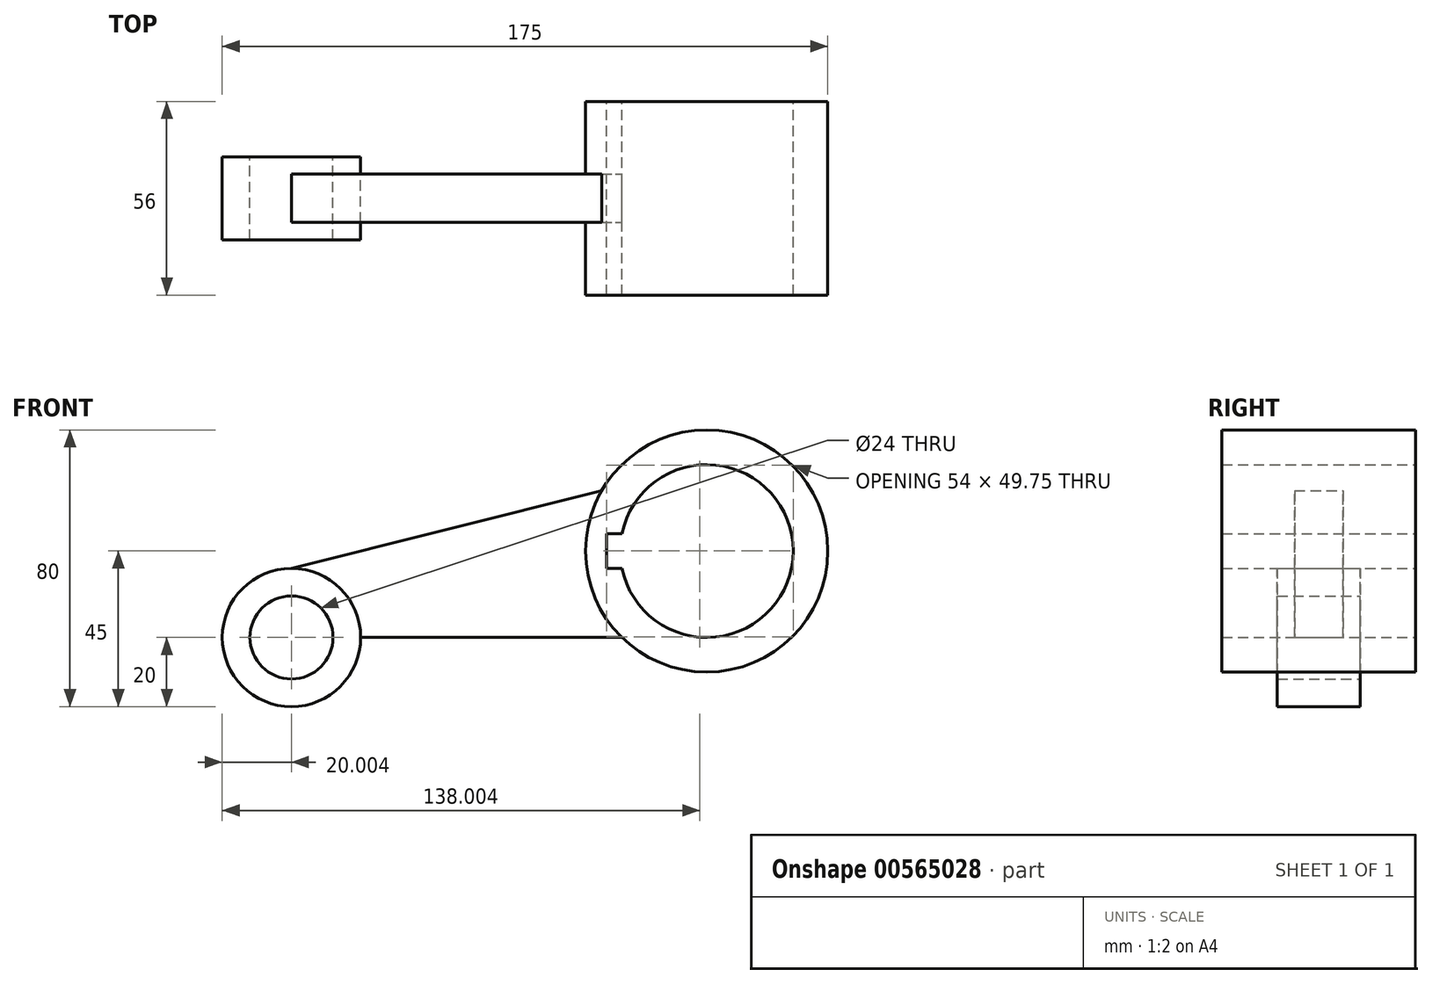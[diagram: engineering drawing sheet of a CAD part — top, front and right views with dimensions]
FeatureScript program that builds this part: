
annotation { "Feature Type Name" : "Feature", "Feature Type Description" : "" }
export const myFeature = defineFeature(function(context is Context, id is Id, definition is map)
    precondition{}
    {
        {
            var Q0;
            Q0=qCreatedBy(makeId("Front.planeOp"),FACE);
            var sketch = newSketch(context, id + "F0", { "sketchPlane" : qUnion([Q0])});
            skLineSegment(sketch, "E0", {"start": v(-29.44, -20) * mm, "end": v(66.07, -20) * mm});
            skCircle(sketch, "E1", {"center": v(-29.44, -20) * mm, "radius": 12 * mm});
            skCircle(sketch, "E2", {"center": v(-29.44, -20) * mm, "radius": 20 * mm});
            skLineSegment(sketch, "E3", {"start": v(90.56, -20) * mm, "end": v(90.56, 30) * mm});
            skLineSegment(sketch, "E4", {"start": v(-29.44, 0) * mm, "end": v(60.2, 22.4) * mm});
            skCircle(sketch, "E5", {"center": v(90.56, 5) * mm, "radius": 35 * mm});
            skCircle(sketch, "E6", {"center": v(90.56, 5) * mm, "radius": 25 * mm});
            skLineSegment(sketch, "E7", {"start": v(90.56, 5) * mm, "end": v(65.56, 5) * mm});
            skLineSegment(sketch, "E8", {"start": v(65.56, 5) * mm, "end": v(61.56, 5) * mm});
            skLineSegment(sketch, "E9", {"start": v(61.56, 5) * mm, "end": v(61.56, 0) * mm});
            skLineSegment(sketch, "E10", {"start": v(61.56, 0) * mm, "end": v(61.56, 10) * mm});
            skLineSegment(sketch, "E11", {"start": v(61.56, 10) * mm, "end": v(66.07, 10) * mm});
            skLineSegment(sketch, "E12", {"start": v(66.07, 10) * mm, "end": v(61.56, 0) * mm});
            skLineSegment(sketch, "E13", {"start": v(61.56, 0) * mm, "end": v(66.07, 0) * mm});
            skSolve(sketch);
        }
        {
            var Q0;
            Q0=makeQuery(id+"F0.imprint","IMPRINT",FACE,{"disambiguationData":[TD([[makeQuery(id+"F0.imprint","IMPRINT",EDGE,{"derivedFrom":sQuery(id+"F0.wireOp",EDGE,"E1")}),-1.0]])]});
            extrude(context, id + "F1", {"entities" : qUnion([Q0]), "depth" : 12 * mm, "offsetDistance" : 25 * mm, "hasSecondDirection" : true, "secondDirectionOppositeDirection" : true, "secondDirectionDepth" : 12 * mm});
        }
        {
            var Q0;
            {var subQ5=sQuery(id+"F0.wireOp",EDGE,"E4");Q0=makeQuery(id+"F0.imprint","IMPRINT",FACE,{"disambiguationData":[TD([[makeQuery(id+"F0.imprint","IMPRINT",EDGE,{"derivedFrom":subQ5}),-1.0]])]});}
            extrude(context, id + "F2", {"entities" : qUnion([Q0]), "operationType" : NewBodyOperationType.ADD, "depth" : 7 * mm, "offsetDistance" : 25 * mm, "hasSecondDirection" : true, "secondDirectionOppositeDirection" : true, "secondDirectionDepth" : 7 * mm});
        }
        {
            var Q0;
            {var subQ4=sQuery(id+"F0.wireOp",EDGE,"E11");Q0=makeQuery(id+"F0.imprint","IMPRINT",FACE,{"disambiguationData":[TD([[makeQuery(id+"F0.imprint","IMPRINT",EDGE,{"derivedFrom":subQ4}),1.0]])]});}
            extrude(context, id + "F3", {"entities" : qUnion([Q0]), "operationType" : NewBodyOperationType.ADD, "depth" : 28 * mm, "offsetDistance" : 25 * mm, "hasSecondDirection" : true, "secondDirectionOppositeDirection" : true, "secondDirectionDepth" : 28 * mm});
        }
    });
